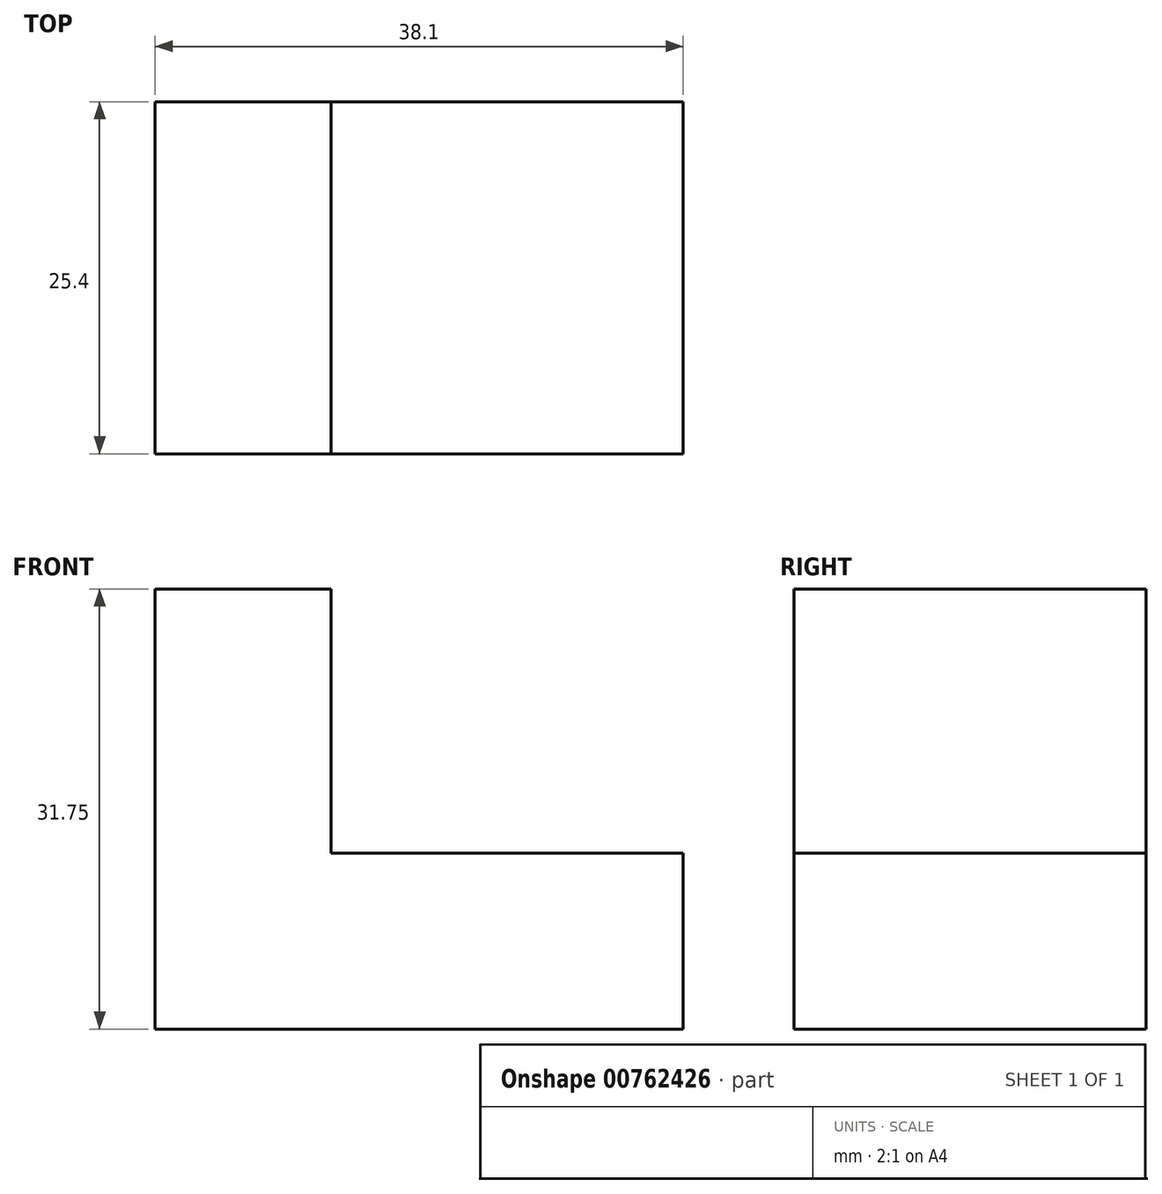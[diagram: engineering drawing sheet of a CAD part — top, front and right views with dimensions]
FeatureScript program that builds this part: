
annotation { "Feature Type Name" : "Feature", "Feature Type Description" : "" }
export const myFeature = defineFeature(function(context is Context, id is Id, definition is map)
    precondition{}
    {
        {
            var Q0;
            Q0=qCreatedBy(makeId("Front.planeOp"),FACE);
            var sketch = newSketch(context, id + "F0", { "sketchPlane" : qUnion([Q0])});
            skLineSegment(sketch, "E0", {"start": v(0, 0) * mm, "end": v(0, 12.7) * mm});
            skLineSegment(sketch, "E1", {"start": v(0, 12.7) * mm, "end": v(-25.4, 12.7) * mm});
            skLineSegment(sketch, "E2", {"start": v(0, 0) * mm, "end": v(-38.1, 0) * mm});
            skLineSegment(sketch, "E3", {"start": v(-38.1, 0) * mm, "end": v(-38.1, 31.75) * mm});
            skLineSegment(sketch, "E4", {"start": v(-25.4, 12.7) * mm, "end": v(-25.4, 31.75) * mm});
            skLineSegment(sketch, "E5", {"start": v(-38.1, 31.75) * mm, "end": v(-25.4, 31.75) * mm});
            skSolve(sketch);
        }
        {
            var Q0;
            Q0=makeQuery(id+"F0.imprint","IMPRINT",FACE,{"disambiguationData":[TD([[makeQuery(id+"F0.imprint","IMPRINT",EDGE,{"derivedFrom":sQuery(id+"F0.wireOp",EDGE,"E0")}),1.0]])]});
            extrude(context, id + "F1", {"entities" : qUnion([Q0]), "depth" : 25.4 * mm, "offsetDistance" : 25.4 * mm});
        }
    });
